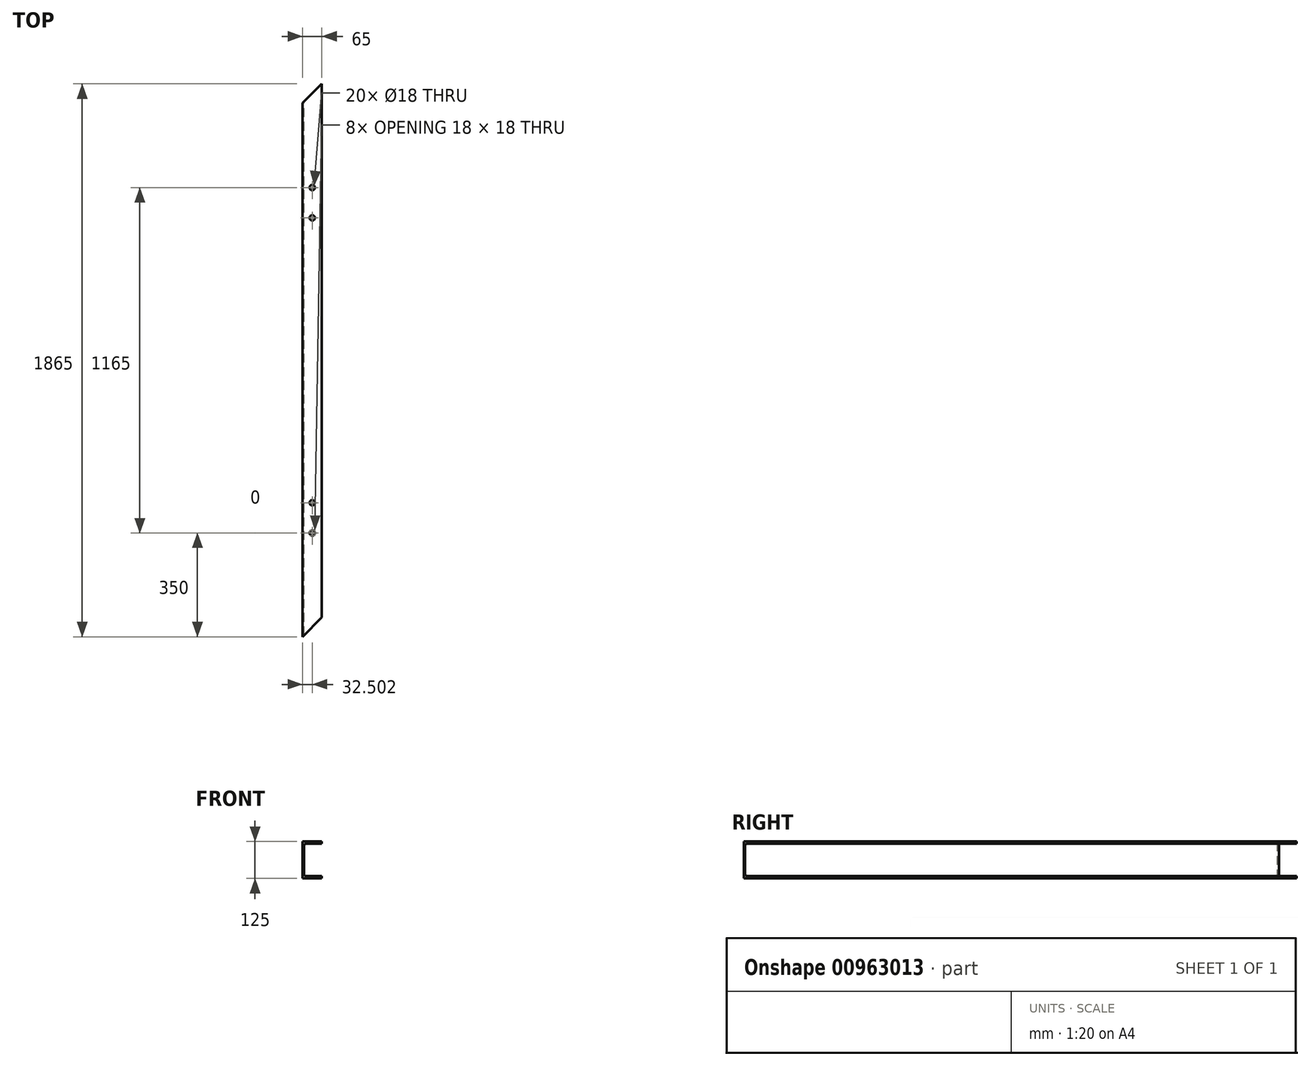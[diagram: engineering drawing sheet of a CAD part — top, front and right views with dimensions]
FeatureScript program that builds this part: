
annotation { "Feature Type Name" : "Feature", "Feature Type Description" : "" }
export const myFeature = defineFeature(function(context is Context, id is Id, definition is map)
    precondition{}
    {
        {
            var Q0;
            Q0=qCreatedBy(makeId("Front.planeOp"),FACE);
            var sketch = newSketch(context, id + "F0", { "sketchPlane" : qUnion([Q0])});
            skLineSegment(sketch, "E0", {"start": v(-25.17, -62.5) * mm, "end": v(-25.17, 62.5) * mm});
            skLineSegment(sketch, "E1", {"start": v(-25.17, 62.5) * mm, "end": v(39.83, 62.5) * mm});
            skLineSegment(sketch, "E2", {"start": v(39.83, 62.5) * mm, "end": v(39.83, 55) * mm});
            skLineSegment(sketch, "E3", {"start": v(39.83, 55) * mm, "end": v(-12.47, 55) * mm});
            skLineSegment(sketch, "E4", {"start": v(-25.17, -62.5) * mm, "end": v(39.83, -62.5) * mm});
            skLineSegment(sketch, "E5", {"start": v(39.83, -62.5) * mm, "end": v(39.83, -55) * mm});
            skLineSegment(sketch, "E6", {"start": v(39.83, -55) * mm, "end": v(-12.47, -55) * mm});
            skLineSegment(sketch, "E7", {"start": v(-20.47, -47) * mm, "end": v(-20.47, 47) * mm});
            skPoint(sketch, "E8.visualSharp", {"position": v(-20.47, 55) * mm});
            skArc(sketch, "E8.filletArc", {"start": v(-12.47, 55) * mm, "mid": v(-18.12, 52.66) * mm, "end": v(-20.47, 47) * mm});
            skPoint(sketch, "E9.visualSharp", {"position": v(-20.47, -55) * mm});
            skArc(sketch, "E9.filletArc", {"start": v(-20.47, -47) * mm, "mid": v(-18.12, -52.66) * mm, "end": v(-12.47, -55) * mm});
            skSolve(sketch);
        }
        {
            var Q0;
            Q0=makeQuery(id+"F0.imprint","IMPRINT",FACE,{"disambiguationData":[TD([[makeQuery(id+"F0.imprint","IMPRINT",EDGE,{"derivedFrom":sQuery(id+"F0.wireOp",EDGE,"E0")}),-1.0]])]});
            extrude(context, id + "F1", {"entities" : qUnion([Q0]), "depth" : 1865 * mm, "offsetDistance" : 25 * mm});
        }
        {
            var Q0;
            Q0=makeQuery(id+"F1.opExtrude","SWEPT_FACE",FACE,{"disambiguationData":[OSD([sQuery(id+"F0.wireOp",EDGE,"E1")])]});
            var sketch = newSketch(context, id + "F2", { "sketchPlane" : qUnion([Q0])});
            skLineSegment(sketch, "E10", {"start": v(-25.17, 0) * mm, "end": v(-25.17, -65) * mm});
            skLineSegment(sketch, "E11", {"start": v(-25.17, -65) * mm, "end": v(39.83, 0) * mm});
            skLineSegment(sketch, "E12", {"start": v(39.83, -1865) * mm, "end": v(39.83, -1800) * mm});
            skLineSegment(sketch, "E13", {"start": v(39.83, -1800) * mm, "end": v(-25.17, -1865) * mm});
            skSolve(sketch);
        }
        {
            var Q0;
            Q0=makeQuery(id+"F2.imprint","IMPRINT",FACE,{"disambiguationData":[TD([[makeQuery(id+"F2.imprint","IMPRINT",EDGE,{"derivedFrom":sQuery(id+"F2.wireOp",EDGE,"E12")}),1.0]])]});
            var Q1;
            Q1=makeQuery(id+"F2.imprint","IMPRINT",FACE,{"disambiguationData":[TD([[makeQuery(id+"F2.imprint","IMPRINT",EDGE,{"derivedFrom":sQuery(id+"F2.wireOp",EDGE,"E10")}),-1.0]])]});
            extrude(context, id + "F3", {"entities" : qUnion([Q0, Q1]), "operationType" : NewBodyOperationType.REMOVE, "endBound" : BoundingType.THROUGH_ALL, "oppositeDirection" : true, "depth" : 25 * mm, "offsetDistance" : 25 * mm});
        }
        {
            var Q0;
            Q0=makeQuery(id+"F1.opExtrude","SWEPT_FACE",FACE,{"disambiguationData":[OSD([sQuery(id+"F0.wireOp",EDGE,"E1")])]});
            var sketch = newSketch(context, id + "F4", { "sketchPlane" : qUnion([Q0])});
            skCircle(sketch, "E14", {"center": v(7.33, -350) * mm, "radius": 9 * mm});
            skCircle(sketch, "E15", {"center": v(7.33, -452) * mm, "radius": 9 * mm});
            skCircle(sketch, "E16", {"center": v(7.33, -1515) * mm, "radius": 9 * mm});
            skCircle(sketch, "E17", {"center": v(7.33, -1413) * mm, "radius": 9 * mm});
            skSolve(sketch);
        }
        {
            var Q0;
            Q0=qSketchRegion(id+"F4",true);
            extrude(context, id + "F5", {"entities" : qUnion([Q0]), "operationType" : NewBodyOperationType.REMOVE, "endBound" : BoundingType.UP_TO_NEXT, "oppositeDirection" : true, "depth" : 25 * mm, "offsetDistance" : 25 * mm});
        }
    });
